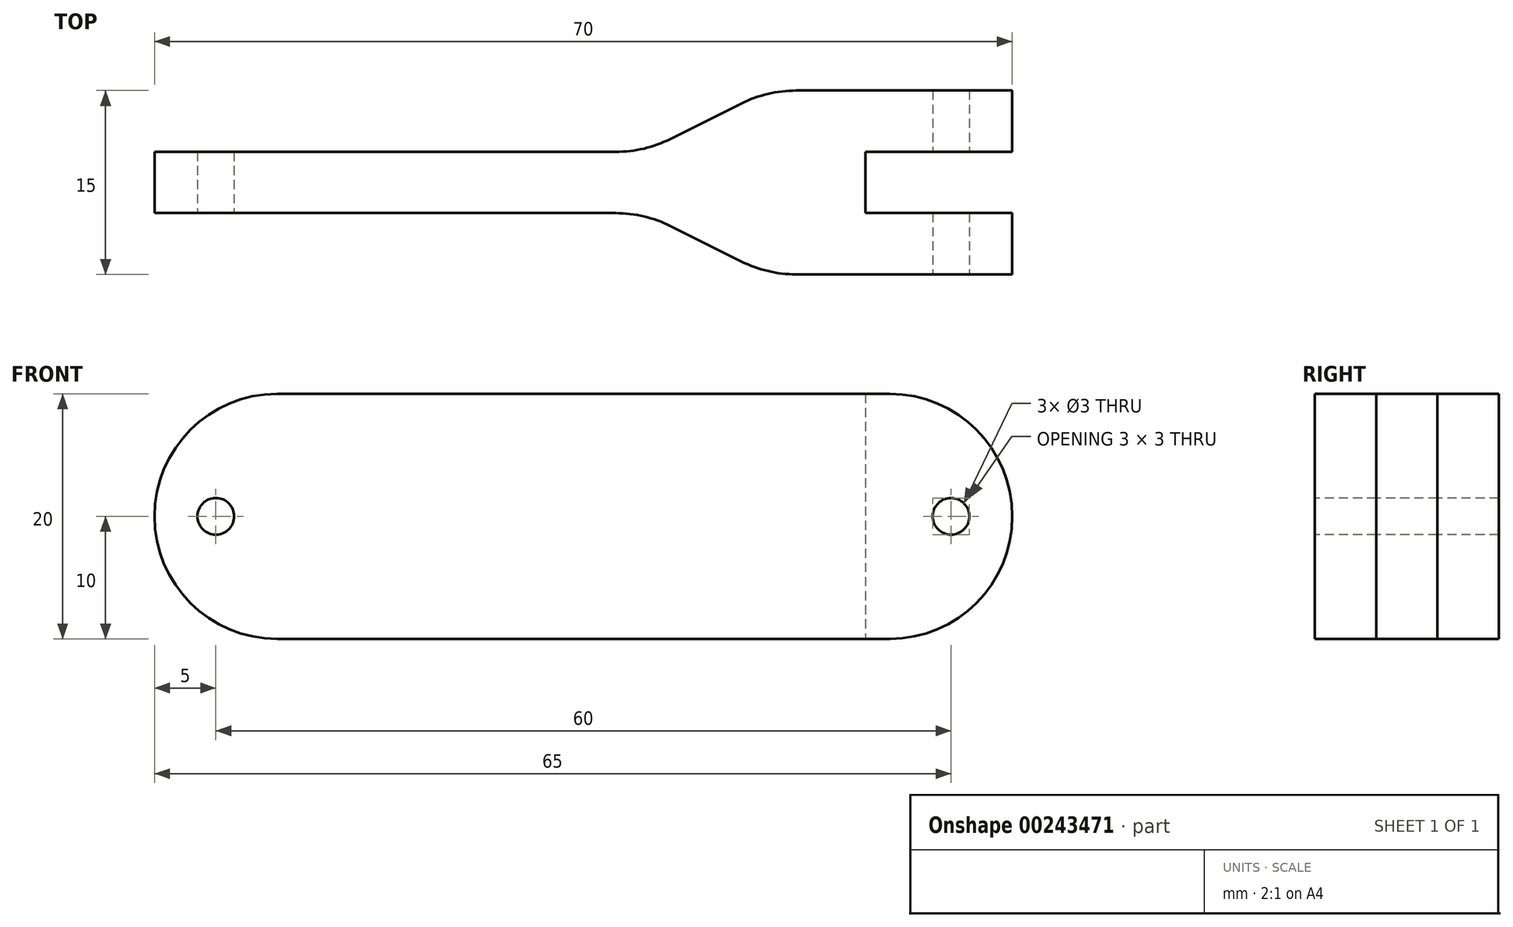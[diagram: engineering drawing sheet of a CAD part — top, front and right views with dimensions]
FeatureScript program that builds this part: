
annotation { "Feature Type Name" : "Feature", "Feature Type Description" : "" }
export const myFeature = defineFeature(function(context is Context, id is Id, definition is map)
    precondition{}
    {
        {
            var Q0;
            Q0=qCreatedBy(makeId("Top.planeOp"),FACE);
            var sketch = newSketch(context, id + "F0", { "sketchPlane" : qUnion([Q0])});
            skLineSegment(sketch, "E0.bottom", {"start": v(0, 0) * mm, "end": v(20, 0) * mm});
            skLineSegment(sketch, "E0.top", {"start": v(0, 15) * mm, "end": v(20, 15) * mm});
            skLineSegment(sketch, "E0.left", {"start": v(0, 0) * mm, "end": v(0, 15) * mm});
            skLineSegment(sketch, "E0.right", {"start": v(20, 0) * mm, "end": v(20, 15) * mm});
            skLineSegment(sketch, "E1.bottom", {"start": v(0, 5) * mm, "end": v(-50, 5) * mm});
            skLineSegment(sketch, "E1.top", {"start": v(0, 10) * mm, "end": v(-50, 10) * mm});
            skLineSegment(sketch, "E1.left", {"start": v(0, 5) * mm, "end": v(0, 10) * mm});
            skLineSegment(sketch, "E1.right", {"start": v(-50, 5) * mm, "end": v(-50, 10) * mm});
            skPoint(sketch, "E2.firstSnap0", {"position": v(20, 7.5) * mm});
            skLineSegment(sketch, "E2.bottom", {"start": v(20, 5) * mm, "end": v(8, 5) * mm});
            skLineSegment(sketch, "E2.top", {"start": v(20, 10) * mm, "end": v(8, 10) * mm});
            skLineSegment(sketch, "E2.left", {"start": v(20, 5) * mm, "end": v(20, 10) * mm});
            skLineSegment(sketch, "E2.right", {"start": v(8, 5) * mm, "end": v(8, 10) * mm});
            skSolve(sketch);
        }
        {
            var Q0;
            Q0=makeQuery(id+"F0.imprint","IMPRINT",FACE,{"disambiguationData":[TD([[makeQuery(id+"F0.imprint","IMPRINT",EDGE,{"derivedFrom":sQuery(id+"F0.wireOp",EDGE,"E1.bottom")}),-1.0]])]});
            var Q1;
            {var subQ4=sQuery(id+"F0.wireOp",EDGE,"E0.bottom");Q1=makeQuery(id+"F0.imprint","IMPRINT",FACE,{"disambiguationData":[TD([[makeQuery(id+"F0.imprint","IMPRINT",EDGE,{"derivedFrom":subQ4}),1.0]])]});}
            extrude(context, id + "F1", {"entities" : qUnion([Q0, Q1]), "depth" : 20 * mm});
        }
        {
            var Q0;
            Q0=makeQuery(id+"F1.opExtrude","SWEPT_FACE",FACE,{"disambiguationData":[OSD([sQuery(id+"F0.wireOp",EDGE,"E1.bottom")])]});
            var sketch = newSketch(context, id + "F2", { "sketchPlane" : qUnion([Q0])});
            skCircle(sketch, "E3", {"center": v(-45, 10) * mm, "radius": 1.5 * mm});
            skPoint(sketch, "E3.centerSnap0", {"position": v(-50, 10) * mm});
            skCircle(sketch, "E4", {"center": v(15, 10) * mm, "radius": 1.5 * mm});
            skLineSegment(sketch, "E5.0", {"start": v(8, 20) * mm, "end": v(8, 0) * mm});
            skArc(sketch, "E6", {"start": v(8, 20) * mm, "mid": v(5.44, 10) * mm, "end": v(8, 0) * mm});
            skSolve(sketch);
        }
        {
            var Q0;
            Q0=makeQuery(id+"F2.imprint","IMPRINT",FACE,{"disambiguationData":[TD([[makeQuery(id+"F2.imprint","IMPRINT",EDGE,{"derivedFrom":sQuery(id+"F2.wireOp",EDGE,"E3")}),1.0]])]});
            var Q1;
            Q1=makeQuery(id+"F2.imprint","IMPRINT",FACE,{"disambiguationData":[TD([[makeQuery(id+"F2.imprint","IMPRINT",EDGE,{"derivedFrom":sQuery(id+"F2.wireOp",EDGE,"E4")}),1.0]])]});
            extrude(context, id + "F3", {"entities" : qUnion([Q0, Q1]), "operationType" : NewBodyOperationType.REMOVE, "oppositeDirection" : true, "depth" : 25 * mm, "symmetric" : true});
        }
        {
            var Q0;
            Q0=makeQuery(id+"F1.opExtrude","CAP_EDGE",EDGE,{"disambiguationData":[OSD([sQuery(id+"F0.wireOp",EDGE,"E1.right")])],"isStart":false});
            var Q1;
            {var subQ0=sQuery(id+"F0.wireOp",EDGE,"E0.right");Q1=makeQuery(id+"F1.opExtrude","CAP_EDGE",EDGE,{"disambiguationData":[OSD([subQ0]),TDD([makeQuery(id+"F0.imprint","IMPRINT",EDGE,{"disambiguationData":[TD([[makeQuery(id+"F0.imprint","INTERSECT",VERTEX,{"derivedFrom":[sQuery(id+"F0.wireOp",EDGE,"E0.top"),subQ0]}),1.0]])],"derivedFrom":subQ0})])],"isStart":false});}
            var Q2;
            {var subQ0=sQuery(id+"F0.wireOp",EDGE,"E0.right");Q2=makeQuery(id+"F1.opExtrude","CAP_EDGE",EDGE,{"disambiguationData":[OSD([subQ0]),TDD([makeQuery(id+"F0.imprint","IMPRINT",EDGE,{"disambiguationData":[TD([[makeQuery(id+"F0.imprint","INTERSECT",VERTEX,{"derivedFrom":[sQuery(id+"F0.wireOp",EDGE,"E0.bottom"),subQ0]}),-1.0]])],"derivedFrom":subQ0})])],"isStart":false});}
            fillet(context, id + "F4", {"entities" : qUnion([Q0, Q1, Q2]), "radius" : 10 * mm, "tangentPropagation" : true, "allowEdgeOverflow" : false});
        }
        {
            var Q0;
            {var subQ0=sQuery(id+"F0.wireOp",EDGE,"E0.right");Q0=makeQuery(id+"F1.opExtrude","CAP_EDGE",EDGE,{"disambiguationData":[OSD([subQ0]),TDD([makeQuery(id+"F0.imprint","IMPRINT",EDGE,{"disambiguationData":[TD([[makeQuery(id+"F0.imprint","INTERSECT",VERTEX,{"derivedFrom":[sQuery(id+"F0.wireOp",EDGE,"E0.bottom"),subQ0]}),-1.0]])],"derivedFrom":subQ0})])],"isStart":true});}
            var Q1;
            {var subQ0=sQuery(id+"F0.wireOp",EDGE,"E0.right");Q1=makeQuery(id+"F1.opExtrude","CAP_EDGE",EDGE,{"disambiguationData":[OSD([subQ0]),TDD([makeQuery(id+"F0.imprint","IMPRINT",EDGE,{"disambiguationData":[TD([[makeQuery(id+"F0.imprint","INTERSECT",VERTEX,{"derivedFrom":[sQuery(id+"F0.wireOp",EDGE,"E0.top"),subQ0]}),1.0]])],"derivedFrom":subQ0})])],"isStart":true});}
            var Q2;
            Q2=makeQuery(id+"F1.opExtrude","CAP_EDGE",EDGE,{"disambiguationData":[OSD([sQuery(id+"F0.wireOp",EDGE,"E1.right")])],"isStart":true});
            fillet(context, id + "F5", {"entities" : qUnion([Q0, Q1, Q2]), "radius" : 10 * mm, "tangentPropagation" : true, "allowEdgeOverflow" : false});
        }
        {
            var Q0;
            Q0=makeQuery(id+"F1.opExtrude","SWEPT_EDGE",EDGE,{"disambiguationData":[OSD([sQuery(id+"F0.wireOp",EDGE,"E0.left"),sQuery(id+"F0.wireOp",EDGE,"E1.bottom"),sQuery(id+"F0.wireOp",EDGE,"E1.left")])]});
            chamfer(context, id + "F6", {"entities" : qUnion([Q0]), "chamferType" : ChamferType.TWO_OFFSETS, "width1" : 5 * mm, "oppositeDirection" : false, "width2" : 10 * mm, "tangentPropagation" : true});
        }
        {
            var Q0;
            Q0=makeQuery(id+"F1.opExtrude","SWEPT_EDGE",EDGE,{"disambiguationData":[OSD([sQuery(id+"F0.wireOp",EDGE,"E0.left"),sQuery(id+"F0.wireOp",EDGE,"E1.top"),sQuery(id+"F0.wireOp",EDGE,"E1.left")])]});
            chamfer(context, id + "F7", {"entities" : qUnion([Q0]), "chamferType" : ChamferType.TWO_OFFSETS, "width1" : 10 * mm, "oppositeDirection" : false, "width2" : 5 * mm, "tangentPropagation" : true});
        }
        {
            var Q0;
            {var subQ0=sQuery(id+"F0.wireOp",EDGE,"E1.bottom");Q0=makeQuery(id+"F6.opChamfer","BLEND_EDGE",EDGE,{"blendedFrom":[makeQuery(id+"F1.opExtrude","SWEPT_EDGE",EDGE,{"disambiguationData":[OSD([sQuery(id+"F0.wireOp",EDGE,"E0.left"),subQ0,sQuery(id+"F0.wireOp",EDGE,"E1.left")])]}),makeQuery(id+"F1.opExtrude","SWEPT_FACE",FACE,{"disambiguationData":[OSD([subQ0])]})],"blendedInto":[makeQuery(id+"F1.opExtrude","SWEPT_FACE",FACE,{"disambiguationData":[OSD([subQ0])]})]});}
            var Q1;
            Q1=makeQuery(id+"F6.opChamfer","BLEND_EDGE",EDGE,{"blendedFrom":[makeQuery(id+"F1.opExtrude","SWEPT_EDGE",EDGE,{"disambiguationData":[OSD([sQuery(id+"F0.wireOp",EDGE,"E0.left"),sQuery(id+"F0.wireOp",EDGE,"E1.bottom"),sQuery(id+"F0.wireOp",EDGE,"E1.left")])]}),makeQuery(id+"F1.opExtrude","SWEPT_FACE",FACE,{"disambiguationData":[OSD([sQuery(id+"F0.wireOp",EDGE,"E0.bottom")])]})],"blendedInto":[makeQuery(id+"F1.opExtrude","SWEPT_FACE",FACE,{"disambiguationData":[OSD([sQuery(id+"F0.wireOp",EDGE,"E0.bottom")])]})]});
            var Q2;
            Q2=makeQuery(id+"F7.opChamfer","BLEND_EDGE",EDGE,{"blendedFrom":[makeQuery(id+"F1.opExtrude","SWEPT_EDGE",EDGE,{"disambiguationData":[OSD([sQuery(id+"F0.wireOp",EDGE,"E0.left"),sQuery(id+"F0.wireOp",EDGE,"E1.top"),sQuery(id+"F0.wireOp",EDGE,"E1.left")])]}),makeQuery(id+"F1.opExtrude","SWEPT_FACE",FACE,{"disambiguationData":[OSD([sQuery(id+"F0.wireOp",EDGE,"E0.top")])]})],"blendedInto":[makeQuery(id+"F1.opExtrude","SWEPT_FACE",FACE,{"disambiguationData":[OSD([sQuery(id+"F0.wireOp",EDGE,"E0.top")])]})]});
            var Q3;
            {var subQ0=sQuery(id+"F0.wireOp",EDGE,"E1.top");Q3=makeQuery(id+"F7.opChamfer","BLEND_EDGE",EDGE,{"blendedFrom":[makeQuery(id+"F1.opExtrude","SWEPT_EDGE",EDGE,{"disambiguationData":[OSD([sQuery(id+"F0.wireOp",EDGE,"E0.left"),subQ0,sQuery(id+"F0.wireOp",EDGE,"E1.left")])]}),makeQuery(id+"F1.opExtrude","SWEPT_FACE",FACE,{"disambiguationData":[OSD([subQ0])]})],"blendedInto":[makeQuery(id+"F1.opExtrude","SWEPT_FACE",FACE,{"disambiguationData":[OSD([subQ0])]})]});}
            fillet(context, id + "F8", {"entities" : qUnion([Q0, Q1, Q2, Q3]), "radius" : 10 * mm, "tangentPropagation" : true, "allowEdgeOverflow" : false});
        }
    });
